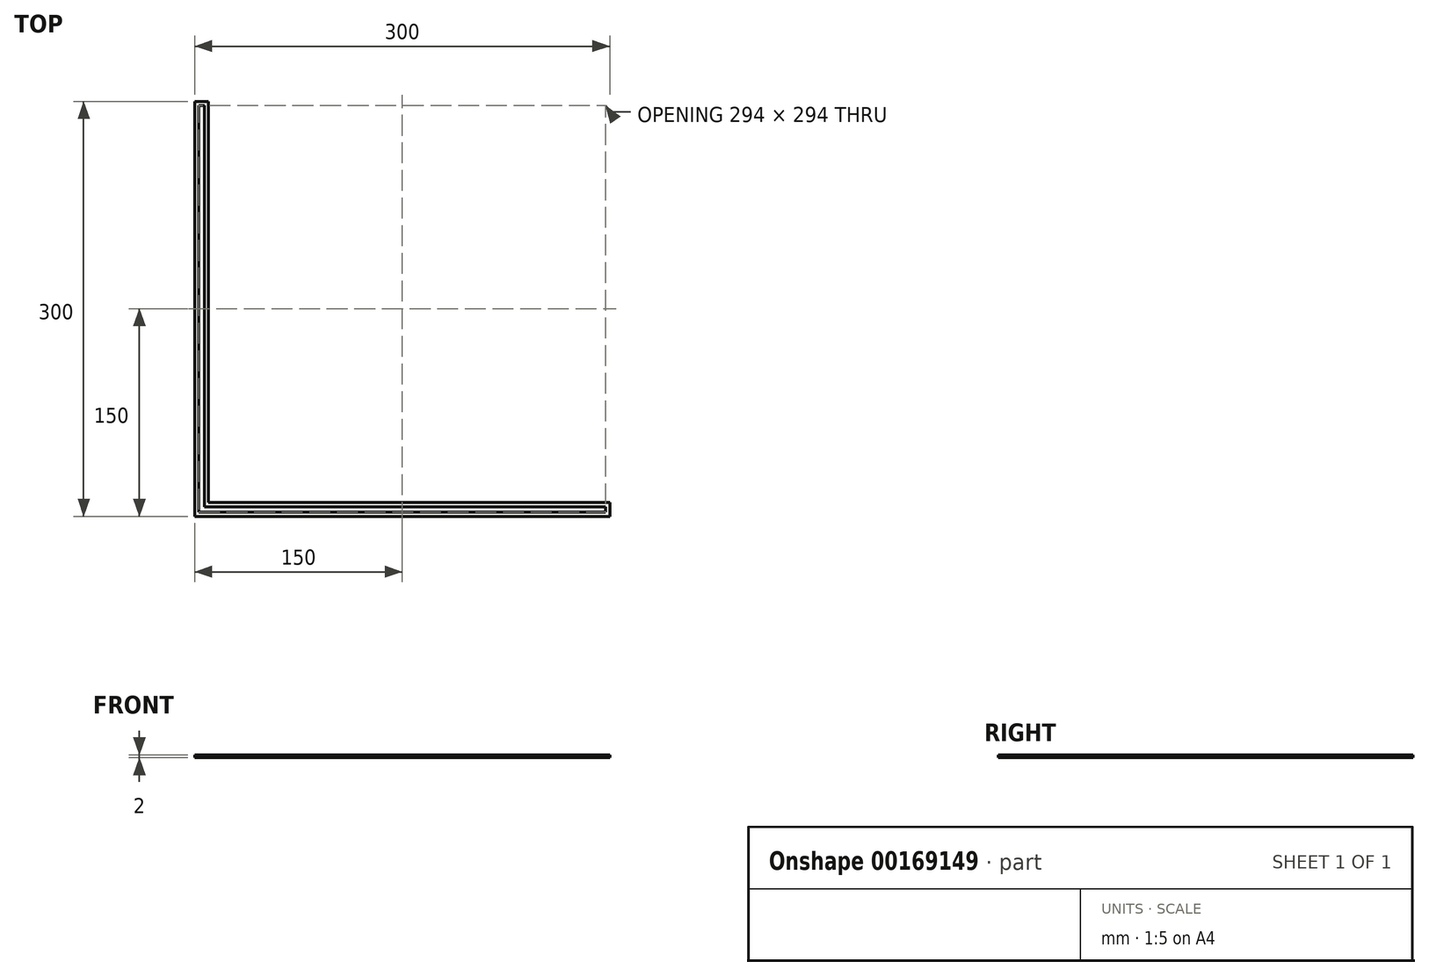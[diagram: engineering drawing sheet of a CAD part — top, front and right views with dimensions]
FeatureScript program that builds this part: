
annotation { "Feature Type Name" : "Feature", "Feature Type Description" : "" }
export const myFeature = defineFeature(function(context is Context, id is Id, definition is map)
    precondition{}
    {
        {
            var Q0;
            Q0=qCreatedBy(makeId("Top.planeOp"),FACE);
            var sketch = newSketch(context, id + "F0", { "sketchPlane" : qUnion([Q0])});
            skLineSegment(sketch, "E0.bottom", {"start": v(0, 0) * mm, "end": v(10, 0) * mm});
            skLineSegment(sketch, "E0.top", {"start": v(0, 300) * mm, "end": v(10, 300) * mm});
            skLineSegment(sketch, "E0.left", {"start": v(0, 0) * mm, "end": v(0, 300) * mm});
            skLineSegment(sketch, "E0.right", {"start": v(10, 10) * mm, "end": v(10, 300) * mm});
            skLineSegment(sketch, "E1.bottom", {"start": v(0, 0) * mm, "end": v(300, 0) * mm});
            skLineSegment(sketch, "E1.top", {"start": v(10, 10) * mm, "end": v(300, 10) * mm});
            skLineSegment(sketch, "E1.left", {"start": v(0, 0) * mm, "end": v(0, 10) * mm});
            skLineSegment(sketch, "E1.right", {"start": v(300, 0) * mm, "end": v(300, 10) * mm});
            skLineSegment(sketch, "E2.0", {"start": v(7, 7) * mm, "end": v(297, 7) * mm});
            skLineSegment(sketch, "E2.1", {"start": v(3, 297) * mm, "end": v(7, 297) * mm});
            skLineSegment(sketch, "E2.2", {"start": v(3, 3) * mm, "end": v(3, 297) * mm});
            skLineSegment(sketch, "E2.3", {"start": v(7, 7) * mm, "end": v(7, 297) * mm});
            skLineSegment(sketch, "E2.4", {"start": v(3, 3) * mm, "end": v(297, 3) * mm});
            skLineSegment(sketch, "E2.5", {"start": v(297, 3) * mm, "end": v(297, 7) * mm});
            skSolve(sketch);
        }
        {
            var Q0;
            Q0=qSketchRegion(id+"F0",true);
            extrude(context, id + "F1", {"entities" : qUnion([Q0]), "depth" : 2 * mm});
        }
    });
